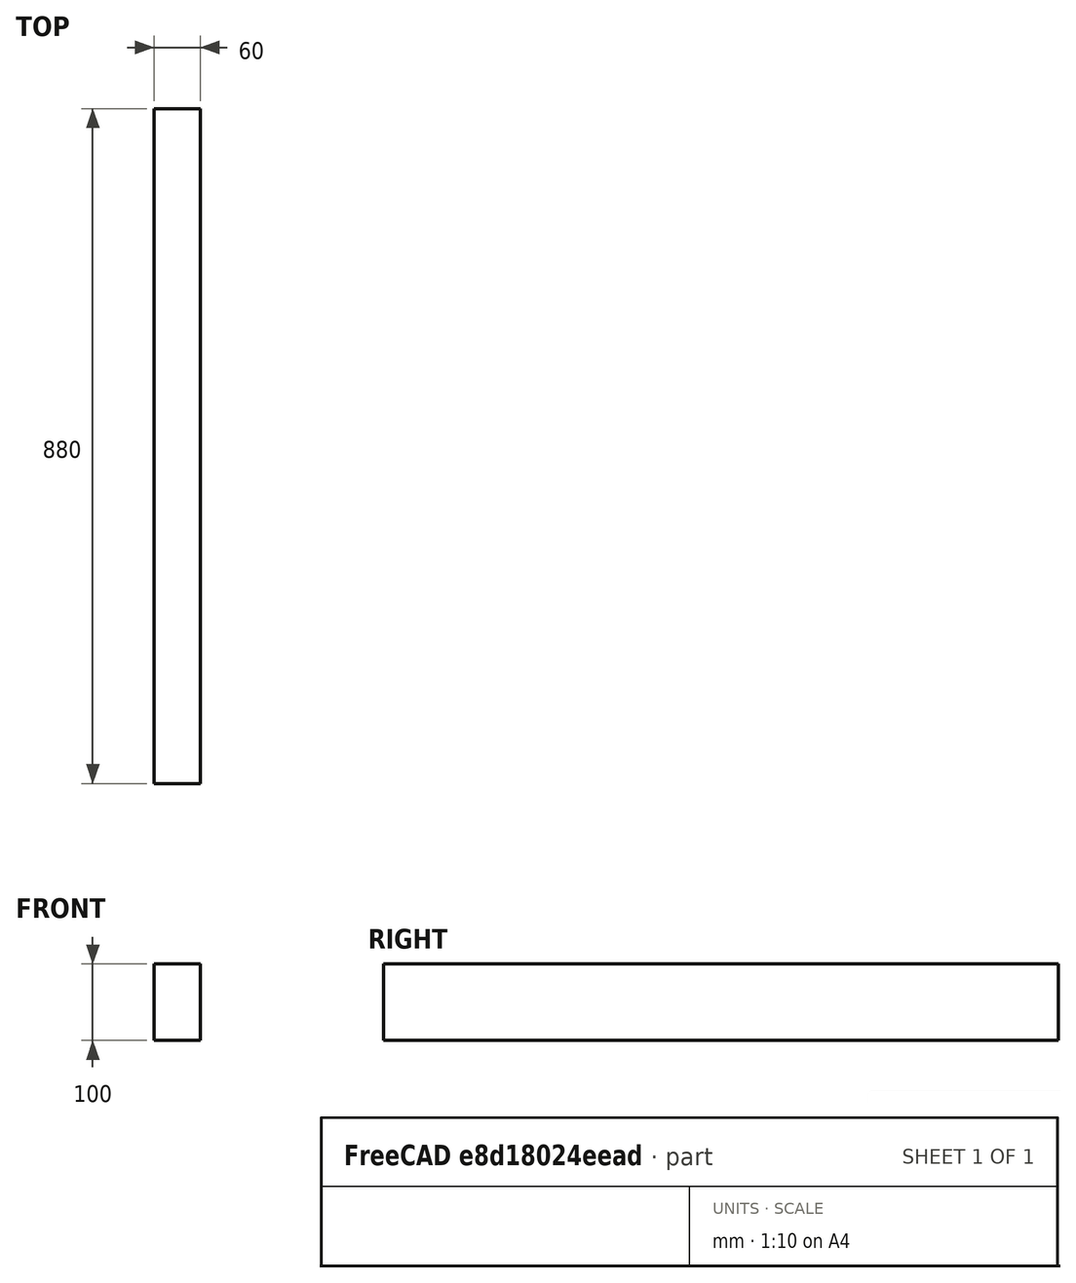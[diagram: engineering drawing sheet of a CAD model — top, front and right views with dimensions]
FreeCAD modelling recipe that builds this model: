
FCSTD DOCUMENT  (FreeCAD 1.0RUnknown)
Label: beam60x100x1000
License: All rights reserved
LicenseURL: https://en.wikipedia.org/wiki/All_rights_reserved
objects: PartDesign::CoordinateSystem×3, Sketcher::SketchObject×1, PartDesign::Pad×1, PartDesign::Body×1, App::Part×1
note: 9 computed .brp shape members not serialized (recipe doc carries the construction recipe); baked Part::Feature solids carry a one-line shape summary decoded from their .brp

FEATURE [Sketcher::SketchObject] Sketch
  ArcFitTolerance = 1e-06
  AttachmentSupport = -> [XZ_Plane]
  FullyConstrained = true
  MakeInternals = false
  MapMode = 5
  Placement = pos=(0,0,0) rot=(1,0,0;1.5708rad)
  sketch-geometry (5):
    g0: LineSegment StartX=-30 StartY=-50 StartZ=0 EndX=30 EndY=-50 EndZ=0
    g1: LineSegment StartX=30 StartY=-50 StartZ=0 EndX=30 EndY=50 EndZ=0
    g2: LineSegment StartX=30 StartY=50 StartZ=0 EndX=-30 EndY=50 EndZ=0
    g3: LineSegment StartX=-30 StartY=50 StartZ=0 EndX=-30 EndY=-50 EndZ=0
    g4: GeomPoint [constr] X=0 Y=0 Z=0
  constraints (12):
    c: Coincident(g0,g1)
    c: Coincident(g1,g2)
    c: Coincident(g2,g3)
    c: Coincident(g3,g0)
    c: Horizontal(g0)
    c: Horizontal(g2)
    c: Vertical(g1)
    c: Vertical(g3)
    c: Symmetric(g2,g0,g4)
    c: Coincident(g4,g-1)
    c: DistanceX(g0,g0) = 60
    c: DistanceY(g3,g3) = 100
FEATURE [PartDesign::Pad] Pad
  Direction = (0,-1,2e-16)
  Length = 880
  Length2 = 10
  Midplane = true
  Placement = pos=(0,0,0) rot=(1,0,0;1.5708rad)
  Profile = -> Sketch
  ReferenceAxis = -> Sketch [N_Axis]
  Refine = true
  Suppressed = false
  Type = 0
FEATURE [PartDesign::Body] Body  label="Körper"
  AllowCompound = false
  Group = -> [Sketch,Pad]
  Origin = -> Origin
  Tip = -> Pad
FEATURE [PartDesign::CoordinateSystem] LCS_Origin
  AttacherType = Attacher::AttachEngine3D
  AttachmentSupport = -> [X_Axis001]
  MapMode = 2
FEATURE [PartDesign::CoordinateSystem] LCS_1
  AttacherType = Attacher::AttachEngine3D
  AttachmentSupport = -> [Pad]
  MapMode = 45
  Placement = pos=(-30,440,-1.95e-13) rot=(0,0,1;0rad)
FEATURE [PartDesign::CoordinateSystem] LCS_2
  AttacherType = Attacher::AttachEngine3D
  AttachmentSupport = -> [Pad]
  MapMode = 45
  Placement = pos=(-30,-440,1.96e-13) rot=(0,0,1;0rad)
FEATURE [App::Part] beam60x100x887  label="beam60x100x800"
  Group = -> [LCS_Origin,Body,LCS_1,LCS_2]
  Origin = -> Origin001
